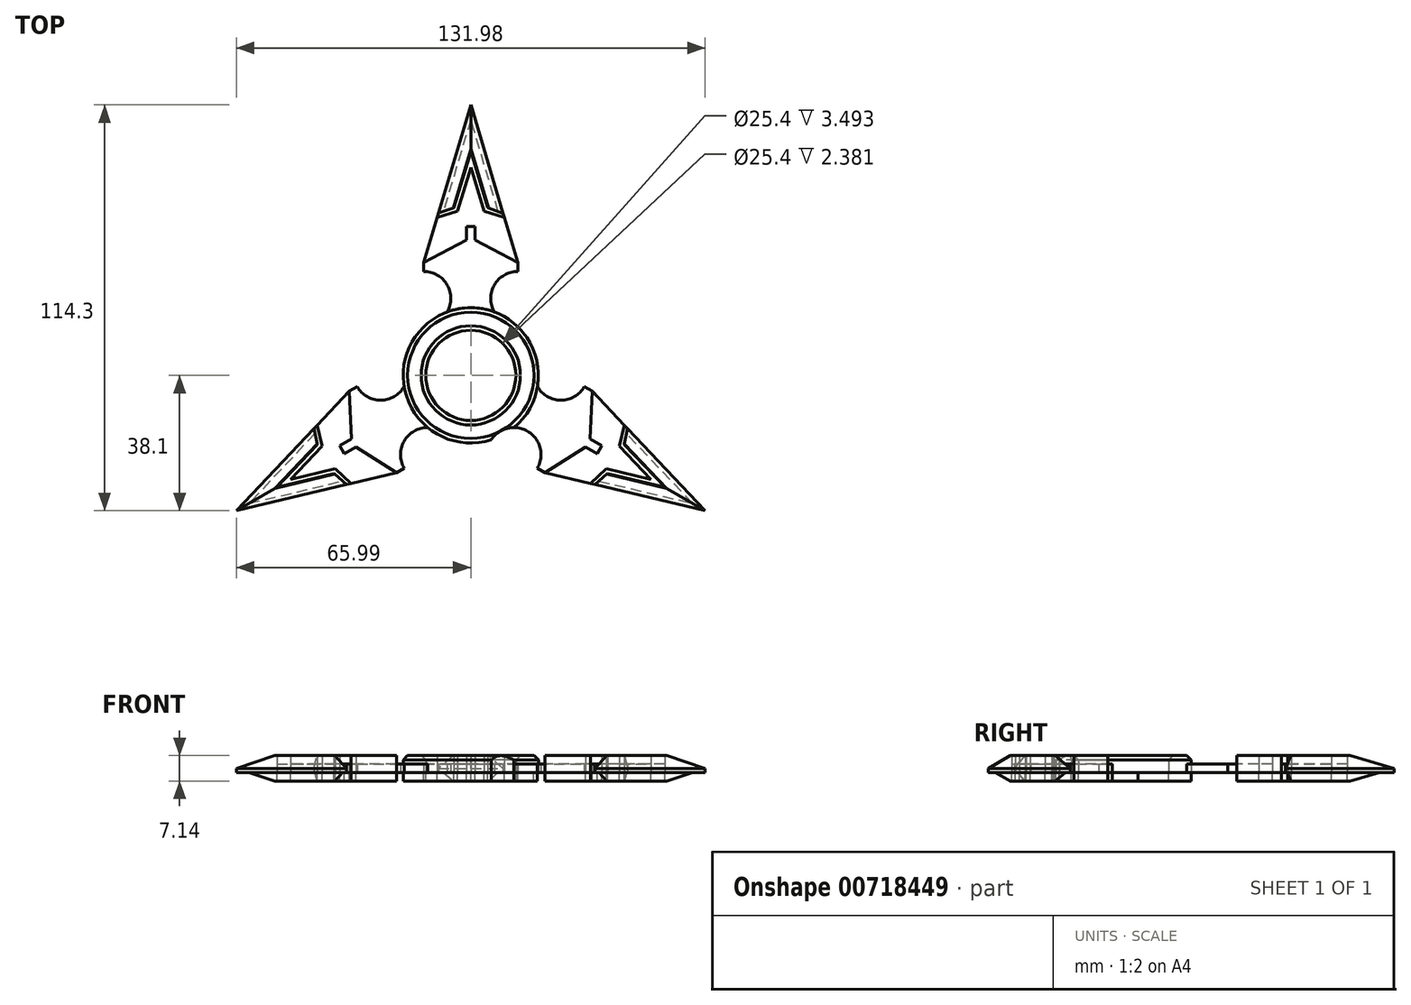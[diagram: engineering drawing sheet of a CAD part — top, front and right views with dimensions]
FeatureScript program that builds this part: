
annotation { "Feature Type Name" : "Feature", "Feature Type Description" : "" }
export const myFeature = defineFeature(function(context is Context, id is Id, definition is map)
    precondition{}
    {
        {
            var Q0;
            Q0=qCreatedBy(makeId("Top.planeOp"),FACE);
            var sketch = newSketch(context, id + "F0", { "sketchPlane" : qUnion([Q0])});
            skCircle(sketch, "E0", {"center": v(0, 0) * mm, "radius": 12.7 * mm});
            skCircle(sketch, "E1", {"center": v(0, 0) * mm, "radius": 19.05 * mm});
            skLineSegment(sketch, "E2", {"start": v(0, 76.2) * mm, "end": v(-13.25, 31.83) * mm});
            skLineSegment(sketch, "E3", {"start": v(13.25, 31.83) * mm, "end": v(0, 76.2) * mm});
            skLineSegment(sketch, "E4", {"start": v(-13.25, 31.83) * mm, "end": v(-13.25, 29.3) * mm});
            skLineSegment(sketch, "E5", {"start": v(13.25, 31.83) * mm, "end": v(13.25, 29.3) * mm});
            skLineSegment(sketch, "E6", {"start": v(0, 0) * mm, "end": v(-4, 18.62) * mm});
            skPoint(sketch, "E7", {"position": v(-12.85, 14.06) * mm});
            skPoint(sketch, "E8", {"position": v(12.85, 14.06) * mm});
            skArc(sketch, "E9", {"start": v(-12.85, 14.06) * mm, "mid": v(-5.63, 21.87) * mm, "end": v(-13.25, 29.3) * mm});
            skArc(sketch, "E10", {"start": v(13.25, 29.3) * mm, "mid": v(5.63, 21.87) * mm, "end": v(12.85, 14.06) * mm});
            skPoint(sketch, "E11", {"position": v(0, 63.05) * mm});
            skPoint(sketch, "E12", {"position": v(-4.73, 47.22) * mm});
            skPoint(sketch, "E13", {"position": v(4.73, 47.22) * mm});
            skPoint(sketch, "E14", {"position": v(-9.1, 45.72) * mm});
            skPoint(sketch, "E15", {"position": v(9.12, 45.67) * mm});
            skLineSegment(sketch, "E16", {"start": v(-9.1, 45.72) * mm, "end": v(-4.73, 47.22) * mm});
            skLineSegment(sketch, "E17", {"start": v(0, 63.05) * mm, "end": v(-4.73, 47.22) * mm});
            skLineSegment(sketch, "E18", {"start": v(0, 63.05) * mm, "end": v(4.73, 47.22) * mm});
            skLineSegment(sketch, "E19", {"start": v(4.73, 47.22) * mm, "end": v(9.12, 45.67) * mm});
            skPoint(sketch, "E20", {"position": v(-9.48, 44.45) * mm});
            skPoint(sketch, "E21", {"position": v(9.48, 44.45) * mm});
            skPoint(sketch, "E22", {"position": v(0, 58.62) * mm});
            skLineSegment(sketch, "E23", {"start": v(-13.25, 31.83) * mm, "end": v(-1.27, 38.1) * mm});
            skLineSegment(sketch, "E24", {"start": v(-1.27, 38.1) * mm, "end": v(-1.27, 41.91) * mm});
            skLineSegment(sketch, "E25", {"start": v(-1.27, 41.91) * mm, "end": v(1.27, 41.91) * mm});
            skLineSegment(sketch, "E26", {"start": v(1.27, 41.91) * mm, "end": v(1.27, 38.1) * mm});
            skLineSegment(sketch, "E27", {"start": v(1.27, 38.1) * mm, "end": v(13.25, 31.83) * mm});
            skLineSegment(sketch, "E28", {"start": v(-9.48, 44.45) * mm, "end": v(-3.7, 46.2) * mm});
            skLineSegment(sketch, "E29", {"start": v(-3.7, 46.2) * mm, "end": v(0, 58.62) * mm});
            skLineSegment(sketch, "E30", {"start": v(0, 58.62) * mm, "end": v(3.7, 46.2) * mm});
            skLineSegment(sketch, "E31", {"start": v(3.7, 46.2) * mm, "end": v(9.48, 44.45) * mm});
            skPoint(sketch, "E32.1.0", {"position": v(-43.23, -14.01) * mm});
            skLineSegment(sketch, "E32.1.1", {"start": v(-66, -38.1) * mm, "end": v(-20.94, -27.39) * mm});
            skLineSegment(sketch, "E32.1.2", {"start": v(-33.63, -17.95) * mm, "end": v(-34.2, -4.44) * mm});
            skPoint(sketch, "E32.1.3", {"position": v(-54.6, -31.53) * mm});
            skLineSegment(sketch, "E32.1.4", {"start": v(-20.94, -27.39) * mm, "end": v(-32.36, -20.15) * mm});
            skLineSegment(sketch, "E32.1.5", {"start": v(-34.2, -4.44) * mm, "end": v(-66, -38.1) * mm});
            skPoint(sketch, "E32.1.6", {"position": v(-33.75, -30.44) * mm});
            skLineSegment(sketch, "E32.1.7", {"start": v(-54.6, -31.53) * mm, "end": v(-38.52, -27.7) * mm});
            skPoint(sketch, "E32.1.8", {"position": v(-38.52, -27.7) * mm});
            skLineSegment(sketch, "E32.1.9", {"start": v(-50.76, -29.3) * mm, "end": v(-41.86, -19.89) * mm});
            skPoint(sketch, "E32.1.10", {"position": v(-44.1, -14.94) * mm});
            skLineSegment(sketch, "E32.1.11", {"start": v(-54.6, -31.53) * mm, "end": v(-43.25, -19.51) * mm});
            skPoint(sketch, "E32.1.12", {"position": v(-50.76, -29.3) * mm});
            skPoint(sketch, "E32.1.13", {"position": v(-43.25, -19.51) * mm});
            skPoint(sketch, "E32.1.14", {"position": v(-35.04, -30.74) * mm});
            skLineSegment(sketch, "E32.1.15", {"start": v(-38.15, -26.3) * mm, "end": v(-50.76, -29.3) * mm});
            skLineSegment(sketch, "E32.1.16", {"start": v(-41.86, -19.89) * mm, "end": v(-43.23, -14.01) * mm});
            skLineSegment(sketch, "E32.1.17", {"start": v(-36.93, -19.86) * mm, "end": v(-33.63, -17.95) * mm});
            skLineSegment(sketch, "E32.1.18", {"start": v(-43.25, -19.51) * mm, "end": v(-44.1, -14.94) * mm});
            skLineSegment(sketch, "E32.1.19", {"start": v(-33.75, -30.44) * mm, "end": v(-38.15, -26.3) * mm});
            skLineSegment(sketch, "E32.1.20", {"start": v(-35.04, -30.74) * mm, "end": v(-38.52, -27.7) * mm});
            skLineSegment(sketch, "E32.1.21", {"start": v(-35.66, -22.05) * mm, "end": v(-36.93, -19.86) * mm});
            skLineSegment(sketch, "E32.1.22", {"start": v(-32.36, -20.15) * mm, "end": v(-35.66, -22.05) * mm});
            skLineSegment(sketch, "E32.1.23", {"start": v(-34.2, -4.44) * mm, "end": v(-32, -3.17) * mm});
            skLineSegment(sketch, "E32.1.24", {"start": v(-20.94, -27.39) * mm, "end": v(-18.74, -26.12) * mm});
            skArc(sketch, "E32.1.25", {"start": v(-32, -3.17) * mm, "mid": v(-21.75, -6.06) * mm, "end": v(-18.6, 4.1) * mm});
            skArc(sketch, "E32.1.26", {"start": v(-5.75, -18.16) * mm, "mid": v(-16.12, -15.81) * mm, "end": v(-18.74, -26.12) * mm});
            skPoint(sketch, "E32.2.0", {"position": v(33.75, -30.44) * mm});
            skLineSegment(sketch, "E32.2.1", {"start": v(66, -38.1) * mm, "end": v(34.2, -4.44) * mm});
            skLineSegment(sketch, "E32.2.2", {"start": v(32.36, -20.15) * mm, "end": v(20.94, -27.39) * mm});
            skPoint(sketch, "E32.2.3", {"position": v(54.6, -31.53) * mm});
            skLineSegment(sketch, "E32.2.4", {"start": v(34.2, -4.44) * mm, "end": v(33.63, -17.95) * mm});
            skLineSegment(sketch, "E32.2.5", {"start": v(20.94, -27.39) * mm, "end": v(66, -38.1) * mm});
            skPoint(sketch, "E32.2.6", {"position": v(43.23, -14.01) * mm});
            skLineSegment(sketch, "E32.2.7", {"start": v(54.6, -31.53) * mm, "end": v(43.25, -19.51) * mm});
            skPoint(sketch, "E32.2.8", {"position": v(43.25, -19.51) * mm});
            skLineSegment(sketch, "E32.2.9", {"start": v(50.76, -29.3) * mm, "end": v(38.15, -26.3) * mm});
            skPoint(sketch, "E32.2.10", {"position": v(35, -30.73) * mm});
            skLineSegment(sketch, "E32.2.11", {"start": v(54.6, -31.53) * mm, "end": v(38.52, -27.7) * mm});
            skPoint(sketch, "E32.2.12", {"position": v(50.76, -29.3) * mm});
            skPoint(sketch, "E32.2.13", {"position": v(38.52, -27.7) * mm});
            skPoint(sketch, "E32.2.14", {"position": v(44.15, -14.98) * mm});
            skLineSegment(sketch, "E32.2.15", {"start": v(41.86, -19.89) * mm, "end": v(50.76, -29.3) * mm});
            skLineSegment(sketch, "E32.2.16", {"start": v(38.15, -26.3) * mm, "end": v(33.75, -30.44) * mm});
            skLineSegment(sketch, "E32.2.17", {"start": v(35.66, -22.05) * mm, "end": v(32.36, -20.15) * mm});
            skLineSegment(sketch, "E32.2.18", {"start": v(38.52, -27.7) * mm, "end": v(35, -30.73) * mm});
            skLineSegment(sketch, "E32.2.19", {"start": v(43.23, -14.01) * mm, "end": v(41.86, -19.89) * mm});
            skLineSegment(sketch, "E32.2.20", {"start": v(44.15, -14.98) * mm, "end": v(43.25, -19.51) * mm});
            skLineSegment(sketch, "E32.2.21", {"start": v(36.93, -19.86) * mm, "end": v(35.66, -22.05) * mm});
            skLineSegment(sketch, "E32.2.22", {"start": v(33.63, -17.95) * mm, "end": v(36.93, -19.86) * mm});
            skLineSegment(sketch, "E32.2.23", {"start": v(20.94, -27.39) * mm, "end": v(18.74, -26.12) * mm});
            skLineSegment(sketch, "E32.2.24", {"start": v(34.2, -4.44) * mm, "end": v(32, -3.17) * mm});
            skArc(sketch, "E32.2.25", {"start": v(18.74, -26.12) * mm, "mid": v(16.12, -15.81) * mm, "end": v(5.75, -18.16) * mm});
            skArc(sketch, "E32.2.26", {"start": v(18.6, 4.1) * mm, "mid": v(21.75, -6.06) * mm, "end": v(32, -3.17) * mm});
            skCircle(sketch, "E33", {"center": v(228.68, 14.43) * mm, "radius": 12.7 * mm});
            skCircle(sketch, "E34", {"center": v(228.68, 14.43) * mm, "radius": 19.05 * mm});
            skLineSegment(sketch, "E35", {"start": v(228.68, 90.63) * mm, "end": v(215.43, 46.27) * mm});
            skLineSegment(sketch, "E36", {"start": v(241.93, 46.27) * mm, "end": v(228.68, 90.63) * mm});
            skLineSegment(sketch, "E37", {"start": v(215.43, 46.27) * mm, "end": v(215.43, 43.73) * mm});
            skLineSegment(sketch, "E38", {"start": v(241.93, 46.27) * mm, "end": v(241.93, 43.73) * mm});
            skPoint(sketch, "E39", {"position": v(215.83, 28.5) * mm});
            skPoint(sketch, "E40", {"position": v(241.53, 28.5) * mm});
            skArc(sketch, "E41", {"start": v(215.83, 28.5) * mm, "mid": v(223.05, 36.3) * mm, "end": v(215.43, 43.73) * mm});
            skArc(sketch, "E42", {"start": v(241.93, 43.73) * mm, "mid": v(234.3, 36.3) * mm, "end": v(241.53, 28.5) * mm});
            skPoint(sketch, "E43", {"position": v(228.68, 77.49) * mm});
            skPoint(sketch, "E44", {"position": v(223.95, 61.65) * mm});
            skPoint(sketch, "E45", {"position": v(233.4, 61.65) * mm});
            skPoint(sketch, "E46", {"position": v(219.58, 60.15) * mm});
            skPoint(sketch, "E47", {"position": v(237.8, 60.1) * mm});
            skLineSegment(sketch, "E48", {"start": v(219.58, 60.15) * mm, "end": v(223.95, 61.65) * mm});
            skLineSegment(sketch, "E49", {"start": v(228.68, 77.49) * mm, "end": v(223.95, 61.65) * mm});
            skLineSegment(sketch, "E50", {"start": v(228.68, 77.49) * mm, "end": v(233.4, 61.65) * mm});
            skLineSegment(sketch, "E51", {"start": v(233.4, 61.65) * mm, "end": v(237.8, 60.1) * mm});
            skPoint(sketch, "E52", {"position": v(219.2, 58.88) * mm});
            skPoint(sketch, "E53", {"position": v(238.16, 58.88) * mm});
            skPoint(sketch, "E54", {"position": v(228.68, 73.05) * mm});
            skLineSegment(sketch, "E55", {"start": v(215.43, 46.27) * mm, "end": v(227.4, 52.53) * mm});
            skLineSegment(sketch, "E56", {"start": v(227.4, 52.53) * mm, "end": v(227.4, 56.34) * mm});
            skLineSegment(sketch, "E57", {"start": v(227.4, 56.34) * mm, "end": v(229.95, 56.34) * mm});
            skLineSegment(sketch, "E58", {"start": v(229.95, 56.34) * mm, "end": v(229.95, 52.53) * mm});
            skLineSegment(sketch, "E59", {"start": v(229.95, 52.53) * mm, "end": v(241.93, 46.27) * mm});
            skLineSegment(sketch, "E60", {"start": v(219.2, 58.88) * mm, "end": v(224.97, 60.63) * mm});
            skLineSegment(sketch, "E61", {"start": v(224.97, 60.63) * mm, "end": v(228.68, 73.05) * mm});
            skLineSegment(sketch, "E62", {"start": v(228.68, 73.05) * mm, "end": v(232.39, 60.63) * mm});
            skLineSegment(sketch, "E63", {"start": v(232.39, 60.63) * mm, "end": v(238.16, 58.88) * mm});
            skPoint(sketch, "E64.1.0", {"position": v(185.44, 0.42) * mm});
            skLineSegment(sketch, "E64.1.1", {"start": v(162.69, -23.67) * mm, "end": v(207.73, -12.95) * mm});
            skLineSegment(sketch, "E64.1.2", {"start": v(195.05, -3.52) * mm, "end": v(194.49, 10) * mm});
            skPoint(sketch, "E64.1.3", {"position": v(174.07, -17.1) * mm});
            skLineSegment(sketch, "E64.1.4", {"start": v(207.73, -12.95) * mm, "end": v(196.32, -5.72) * mm});
            skLineSegment(sketch, "E64.1.5", {"start": v(194.49, 10) * mm, "end": v(162.69, -23.67) * mm});
            skPoint(sketch, "E64.1.6", {"position": v(194.92, -16) * mm});
            skLineSegment(sketch, "E64.1.7", {"start": v(174.07, -17.1) * mm, "end": v(190.15, -13.27) * mm});
            skPoint(sketch, "E64.1.8", {"position": v(190.15, -13.27) * mm});
            skLineSegment(sketch, "E64.1.9", {"start": v(177.92, -14.87) * mm, "end": v(186.82, -5.45) * mm});
            skPoint(sketch, "E64.1.10", {"position": v(184.57, -0.5) * mm});
            skLineSegment(sketch, "E64.1.11", {"start": v(174.07, -17.1) * mm, "end": v(185.42, -5.08) * mm});
            skPoint(sketch, "E64.1.12", {"position": v(177.92, -14.87) * mm});
            skPoint(sketch, "E64.1.13", {"position": v(185.42, -5.08) * mm});
            skPoint(sketch, "E64.1.14", {"position": v(193.63, -16.3) * mm});
            skLineSegment(sketch, "E64.1.15", {"start": v(190.52, -11.88) * mm, "end": v(177.92, -14.87) * mm});
            skLineSegment(sketch, "E64.1.16", {"start": v(186.82, -5.45) * mm, "end": v(185.44, 0.42) * mm});
            skLineSegment(sketch, "E64.1.17", {"start": v(191.75, -5.42) * mm, "end": v(195.05, -3.52) * mm});
            skLineSegment(sketch, "E64.1.18", {"start": v(185.42, -5.08) * mm, "end": v(184.57, -0.5) * mm});
            skLineSegment(sketch, "E64.1.19", {"start": v(194.92, -16) * mm, "end": v(190.52, -11.88) * mm});
            skLineSegment(sketch, "E64.1.20", {"start": v(193.63, -16.3) * mm, "end": v(190.15, -13.27) * mm});
            skLineSegment(sketch, "E64.1.21", {"start": v(193.02, -7.62) * mm, "end": v(191.75, -5.42) * mm});
            skLineSegment(sketch, "E64.1.22", {"start": v(196.32, -5.72) * mm, "end": v(193.02, -7.62) * mm});
            skLineSegment(sketch, "E64.1.23", {"start": v(194.49, 10) * mm, "end": v(196.69, 11.26) * mm});
            skLineSegment(sketch, "E64.1.24", {"start": v(207.73, -12.95) * mm, "end": v(209.93, -11.68) * mm});
            skArc(sketch, "E64.1.25", {"start": v(196.69, 11.26) * mm, "mid": v(206.92, 8.38) * mm, "end": v(210.07, 18.53) * mm});
            skArc(sketch, "E64.1.26", {"start": v(222.93, -3.73) * mm, "mid": v(212.55, -1.38) * mm, "end": v(209.93, -11.68) * mm});
            skPoint(sketch, "E64.2.0", {"position": v(262.43, -16) * mm});
            skLineSegment(sketch, "E64.2.1", {"start": v(294.67, -23.67) * mm, "end": v(262.87, 10) * mm});
            skLineSegment(sketch, "E64.2.2", {"start": v(261.04, -5.72) * mm, "end": v(249.62, -12.95) * mm});
            skPoint(sketch, "E64.2.3", {"position": v(283.28, -17.1) * mm});
            skLineSegment(sketch, "E64.2.4", {"start": v(262.87, 10) * mm, "end": v(262.3, -3.52) * mm});
            skLineSegment(sketch, "E64.2.5", {"start": v(249.62, -12.95) * mm, "end": v(294.67, -23.67) * mm});
            skPoint(sketch, "E64.2.6", {"position": v(271.91, 0.42) * mm});
            skLineSegment(sketch, "E64.2.7", {"start": v(283.28, -17.1) * mm, "end": v(271.93, -5.08) * mm});
            skPoint(sketch, "E64.2.8", {"position": v(271.93, -5.08) * mm});
            skLineSegment(sketch, "E64.2.9", {"start": v(279.44, -14.87) * mm, "end": v(266.83, -11.88) * mm});
            skPoint(sketch, "E64.2.10", {"position": v(263.67, -16.3) * mm});
            skLineSegment(sketch, "E64.2.11", {"start": v(283.28, -17.1) * mm, "end": v(267.2, -13.27) * mm});
            skPoint(sketch, "E64.2.12", {"position": v(279.44, -14.87) * mm});
            skPoint(sketch, "E64.2.13", {"position": v(267.2, -13.27) * mm});
            skPoint(sketch, "E64.2.14", {"position": v(272.82, -0.54) * mm});
            skLineSegment(sketch, "E64.2.15", {"start": v(270.54, -5.45) * mm, "end": v(279.44, -14.87) * mm});
            skLineSegment(sketch, "E64.2.16", {"start": v(266.83, -11.88) * mm, "end": v(262.43, -16) * mm});
            skLineSegment(sketch, "E64.2.17", {"start": v(264.34, -7.62) * mm, "end": v(261.04, -5.72) * mm});
            skLineSegment(sketch, "E64.2.18", {"start": v(267.2, -13.27) * mm, "end": v(263.67, -16.3) * mm});
            skLineSegment(sketch, "E64.2.19", {"start": v(271.91, 0.42) * mm, "end": v(270.54, -5.45) * mm});
            skLineSegment(sketch, "E64.2.20", {"start": v(272.82, -0.54) * mm, "end": v(271.93, -5.08) * mm});
            skLineSegment(sketch, "E64.2.21", {"start": v(265.6, -5.42) * mm, "end": v(264.34, -7.62) * mm});
            skLineSegment(sketch, "E64.2.22", {"start": v(262.3, -3.52) * mm, "end": v(265.6, -5.42) * mm});
            skLineSegment(sketch, "E64.2.23", {"start": v(249.62, -12.95) * mm, "end": v(247.42, -11.68) * mm});
            skLineSegment(sketch, "E64.2.24", {"start": v(262.87, 10) * mm, "end": v(260.67, 11.26) * mm});
            skArc(sketch, "E64.2.25", {"start": v(247.42, -11.68) * mm, "mid": v(244.8, -1.38) * mm, "end": v(234.43, -3.73) * mm});
            skArc(sketch, "E64.2.26", {"start": v(247.28, 18.53) * mm, "mid": v(250.43, 8.38) * mm, "end": v(260.67, 11.26) * mm});
            skSolve(sketch);
        }
        {
            var Q0;
            Q0=makeQuery(id+"F0.imprint","IMPRINT",FACE,{"disambiguationData":[TD([[makeQuery(id+"F0.imprint","IMPRINT",EDGE,{"derivedFrom":sQuery(id+"F0.wireOp",EDGE,"E32.2.2")}),-1.0]])]});
            var Q1;
            Q1=makeQuery(id+"F0.imprint","IMPRINT",FACE,{"disambiguationData":[TD([[makeQuery(id+"F0.imprint","IMPRINT",EDGE,{"derivedFrom":sQuery(id+"F0.wireOp",EDGE,"E32.1.2")}),-1.0]])]});
            var Q2;
            {var subQ5=sQuery(id+"F0.wireOp",EDGE,"E4");Q2=makeQuery(id+"F0.imprint","IMPRINT",FACE,{"disambiguationData":[TD([[makeQuery(id+"F0.imprint","IMPRINT",EDGE,{"derivedFrom":subQ5}),1.0]])]});}
            var Q3;
            {var subQ1=sQuery(id+"F0.wireOp",EDGE,"E16");Q3=makeQuery(id+"F0.imprint","IMPRINT",FACE,{"disambiguationData":[TD([[makeQuery(id+"F0.imprint","IMPRINT",EDGE,{"derivedFrom":subQ1}),-1.0]])]});}
            var Q4;
            Q4=makeQuery(id+"F0.imprint","IMPRINT",FACE,{"disambiguationData":[TD([[makeQuery(id+"F0.imprint","IMPRINT",EDGE,{"derivedFrom":sQuery(id+"F0.wireOp",EDGE,"E32.2.7")}),1.0]])]});
            var Q5;
            Q5=makeQuery(id+"F0.imprint","IMPRINT",FACE,{"disambiguationData":[TD([[makeQuery(id+"F0.imprint","IMPRINT",EDGE,{"derivedFrom":sQuery(id+"F0.wireOp",EDGE,"E32.1.7")}),1.0]])]});
            extrude(context, id + "F1", {"entities" : qUnion([Q0, Q1, Q2, Q3, Q4, Q5]), "depth" : 2.38 * mm, "offsetDistance" : 25.4 * mm});
        }
        {
            var Q0;
            {var subQ2=sQuery(id+"F0.wireOp",EDGE,"E23");Q0=makeQuery(id+"F0.imprint","IMPRINT",FACE,{"disambiguationData":[TD([[makeQuery(id+"F0.imprint","IMPRINT",EDGE,{"derivedFrom":subQ2}),1.0]])]});}
            var Q1;
            {var subQ0=sQuery(id+"F0.wireOp",EDGE,"E16");Q1=makeQuery(id+"F0.imprint","IMPRINT",FACE,{"disambiguationData":[TD([[makeQuery(id+"F0.imprint","IMPRINT",EDGE,{"derivedFrom":subQ0}),1.0]])]});}
            var Q2;
            {var subQ4=sQuery(id+"F0.wireOp",EDGE,"E32.2.2");Q2=makeQuery(id+"F0.imprint","IMPRINT",FACE,{"disambiguationData":[TD([[makeQuery(id+"F0.imprint","IMPRINT",EDGE,{"derivedFrom":subQ4}),1.0]])]});}
            var Q3;
            Q3=makeQuery(id+"F0.imprint","IMPRINT",FACE,{"disambiguationData":[TD([[makeQuery(id+"F0.imprint","IMPRINT",EDGE,{"derivedFrom":sQuery(id+"F0.wireOp",EDGE,"E32.2.7")}),-1.0]])]});
            var Q4;
            Q4=makeQuery(id+"F0.imprint","IMPRINT",FACE,{"disambiguationData":[TD([[makeQuery(id+"F0.imprint","IMPRINT",EDGE,{"derivedFrom":sQuery(id+"F0.wireOp",EDGE,"E32.1.7")}),-1.0]])]});
            var Q5;
            {var subQ4=sQuery(id+"F0.wireOp",EDGE,"E32.1.2");Q5=makeQuery(id+"F0.imprint","IMPRINT",FACE,{"disambiguationData":[TD([[makeQuery(id+"F0.imprint","IMPRINT",EDGE,{"derivedFrom":subQ4}),1.0]])]});}
            var Q6;
            Q6=makeQuery(id+"F0.imprint","IMPRINT",FACE,{"disambiguationData":[TD([[makeQuery(id+"F0.imprint","IMPRINT",EDGE,{"derivedFrom":sQuery(id+"F0.wireOp",EDGE,"E0")}),-1.0]])]});
            var Q7;
            {var subQ0=sQuery(id+"F0.wireOp",EDGE,"E32.2.26");var subQ1=sQuery(id+"F0.wireOp",EDGE,"E1");var subQ2=makeQuery(id+"F0.imprint","INTERSECT",VERTEX,{"disambiguationData":[OD(0.0)],"derivedFrom":[subQ1,subQ0]});Q7=makeQuery(id+"F0.imprint","IMPRINT",FACE,{"disambiguationData":[TD([[makeQuery(id+"F0.imprint","IMPRINT",EDGE,{"disambiguationData":[TD([[subQ2,1.0]])],"derivedFrom":subQ1}),1.0]])]});}
            var Q8;
            {var subQ0=sQuery(id+"F0.wireOp",EDGE,"E32.2.25");var subQ1=sQuery(id+"F0.wireOp",EDGE,"E1");var subQ2=makeQuery(id+"F0.imprint","INTERSECT",VERTEX,{"disambiguationData":[OD(0.0)],"derivedFrom":[subQ1,subQ0]});Q8=makeQuery(id+"F0.imprint","IMPRINT",FACE,{"disambiguationData":[TD([[makeQuery(id+"F0.imprint","IMPRINT",EDGE,{"disambiguationData":[TD([[subQ2,-1.0]])],"derivedFrom":subQ1}),1.0]])]});}
            var Q9;
            {var subQ0=sQuery(id+"F0.wireOp",EDGE,"E32.1.26");var subQ1=sQuery(id+"F0.wireOp",EDGE,"E1");var subQ2=makeQuery(id+"F0.imprint","INTERSECT",VERTEX,{"disambiguationData":[OD(0.0)],"derivedFrom":[subQ1,subQ0]});Q9=makeQuery(id+"F0.imprint","IMPRINT",FACE,{"disambiguationData":[TD([[makeQuery(id+"F0.imprint","IMPRINT",EDGE,{"disambiguationData":[TD([[subQ2,1.0]])],"derivedFrom":subQ1}),1.0]])]});}
            var Q10;
            {var subQ0=sQuery(id+"F0.wireOp",EDGE,"E32.1.25");var subQ1=sQuery(id+"F0.wireOp",EDGE,"E1");var subQ2=makeQuery(id+"F0.imprint","INTERSECT",VERTEX,{"disambiguationData":[OD(0.0)],"derivedFrom":[subQ1,subQ0]});Q10=makeQuery(id+"F0.imprint","IMPRINT",FACE,{"disambiguationData":[TD([[makeQuery(id+"F0.imprint","IMPRINT",EDGE,{"disambiguationData":[TD([[subQ2,-1.0]])],"derivedFrom":subQ1}),1.0]])]});}
            var Q11;
            {var subQ0=sQuery(id+"F0.wireOp",EDGE,"E9");var subQ1=sQuery(id+"F0.wireOp",EDGE,"E1");var subQ2=makeQuery(id+"F0.imprint","INTERSECT",VERTEX,{"disambiguationData":[OD(0.0)],"derivedFrom":[subQ1,subQ0]});Q11=makeQuery(id+"F0.imprint","IMPRINT",FACE,{"disambiguationData":[TD([[makeQuery(id+"F0.imprint","IMPRINT",EDGE,{"disambiguationData":[TD([[subQ2,1.0]])],"derivedFrom":subQ1}),1.0]])]});}
            var Q12;
            {var subQ0=sQuery(id+"F0.wireOp",EDGE,"E10");var subQ1=sQuery(id+"F0.wireOp",EDGE,"E1");var subQ2=makeQuery(id+"F0.imprint","INTERSECT",VERTEX,{"disambiguationData":[OD(0.0)],"derivedFrom":[subQ1,subQ0]});Q12=makeQuery(id+"F0.imprint","IMPRINT",FACE,{"disambiguationData":[TD([[makeQuery(id+"F0.imprint","IMPRINT",EDGE,{"disambiguationData":[TD([[subQ2,-1.0]])],"derivedFrom":subQ1}),1.0]])]});}
            extrude(context, id + "F2", {"entities" : qUnion([Q0, Q1, Q2, Q3, Q4, Q5, Q6, Q7, Q8, Q9, Q10, Q11, Q12]), "depth" : 4.76 * mm, "offsetDistance" : 25.4 * mm});
        }
        {
            var Q0;
            Q0=makeQuery(id+"F0.imprint","IMPRINT",FACE,{"disambiguationData":[TD([[makeQuery(id+"F0.imprint","IMPRINT",EDGE,{"derivedFrom":sQuery(id+"F0.wireOp",EDGE,"E0")}),-1.0]])]});
            var Q1;
            {var subQ0=sQuery(id+"F0.wireOp",EDGE,"E32.2.25");var subQ1=sQuery(id+"F0.wireOp",EDGE,"E1");var subQ2=makeQuery(id+"F0.imprint","INTERSECT",VERTEX,{"disambiguationData":[OD(0.0)],"derivedFrom":[subQ1,subQ0]});Q1=makeQuery(id+"F0.imprint","IMPRINT",FACE,{"disambiguationData":[TD([[makeQuery(id+"F0.imprint","IMPRINT",EDGE,{"disambiguationData":[TD([[subQ2,-1.0]])],"derivedFrom":subQ1}),1.0]])]});}
            var Q2;
            {var subQ0=sQuery(id+"F0.wireOp",EDGE,"E32.1.26");var subQ1=sQuery(id+"F0.wireOp",EDGE,"E1");var subQ2=makeQuery(id+"F0.imprint","INTERSECT",VERTEX,{"disambiguationData":[OD(0.0)],"derivedFrom":[subQ1,subQ0]});Q2=makeQuery(id+"F0.imprint","IMPRINT",FACE,{"disambiguationData":[TD([[makeQuery(id+"F0.imprint","IMPRINT",EDGE,{"disambiguationData":[TD([[subQ2,1.0]])],"derivedFrom":subQ1}),1.0]])]});}
            var Q3;
            {var subQ0=sQuery(id+"F0.wireOp",EDGE,"E32.1.25");var subQ1=sQuery(id+"F0.wireOp",EDGE,"E1");var subQ2=makeQuery(id+"F0.imprint","INTERSECT",VERTEX,{"disambiguationData":[OD(0.0)],"derivedFrom":[subQ1,subQ0]});Q3=makeQuery(id+"F0.imprint","IMPRINT",FACE,{"disambiguationData":[TD([[makeQuery(id+"F0.imprint","IMPRINT",EDGE,{"disambiguationData":[TD([[subQ2,-1.0]])],"derivedFrom":subQ1}),1.0]])]});}
            var Q4;
            {var subQ0=sQuery(id+"F0.wireOp",EDGE,"E9");var subQ1=sQuery(id+"F0.wireOp",EDGE,"E1");var subQ2=makeQuery(id+"F0.imprint","INTERSECT",VERTEX,{"disambiguationData":[OD(0.0)],"derivedFrom":[subQ1,subQ0]});Q4=makeQuery(id+"F0.imprint","IMPRINT",FACE,{"disambiguationData":[TD([[makeQuery(id+"F0.imprint","IMPRINT",EDGE,{"disambiguationData":[TD([[subQ2,1.0]])],"derivedFrom":subQ1}),1.0]])]});}
            var Q5;
            {var subQ0=sQuery(id+"F0.wireOp",EDGE,"E10");var subQ1=sQuery(id+"F0.wireOp",EDGE,"E1");var subQ2=makeQuery(id+"F0.imprint","INTERSECT",VERTEX,{"disambiguationData":[OD(0.0)],"derivedFrom":[subQ1,subQ0]});Q5=makeQuery(id+"F0.imprint","IMPRINT",FACE,{"disambiguationData":[TD([[makeQuery(id+"F0.imprint","IMPRINT",EDGE,{"disambiguationData":[TD([[subQ2,-1.0]])],"derivedFrom":subQ1}),1.0]])]});}
            var Q6;
            {var subQ4=sQuery(id+"F0.wireOp",EDGE,"E32.2.2");Q6=makeQuery(id+"F0.imprint","IMPRINT",FACE,{"disambiguationData":[TD([[makeQuery(id+"F0.imprint","IMPRINT",EDGE,{"derivedFrom":subQ4}),1.0]])]});}
            var Q7;
            Q7=makeQuery(id+"F0.imprint","IMPRINT",FACE,{"disambiguationData":[TD([[makeQuery(id+"F0.imprint","IMPRINT",EDGE,{"derivedFrom":sQuery(id+"F0.wireOp",EDGE,"E32.2.7")}),-1.0]])]});
            var Q8;
            {var subQ4=sQuery(id+"F0.wireOp",EDGE,"E32.1.2");Q8=makeQuery(id+"F0.imprint","IMPRINT",FACE,{"disambiguationData":[TD([[makeQuery(id+"F0.imprint","IMPRINT",EDGE,{"derivedFrom":subQ4}),1.0]])]});}
            var Q9;
            Q9=makeQuery(id+"F0.imprint","IMPRINT",FACE,{"disambiguationData":[TD([[makeQuery(id+"F0.imprint","IMPRINT",EDGE,{"derivedFrom":sQuery(id+"F0.wireOp",EDGE,"E32.1.7")}),-1.0]])]});
            var Q10;
            {var subQ2=sQuery(id+"F0.wireOp",EDGE,"E23");Q10=makeQuery(id+"F0.imprint","IMPRINT",FACE,{"disambiguationData":[TD([[makeQuery(id+"F0.imprint","IMPRINT",EDGE,{"derivedFrom":subQ2}),1.0]])]});}
            var Q11;
            {var subQ0=sQuery(id+"F0.wireOp",EDGE,"E16");Q11=makeQuery(id+"F0.imprint","IMPRINT",FACE,{"disambiguationData":[TD([[makeQuery(id+"F0.imprint","IMPRINT",EDGE,{"derivedFrom":subQ0}),1.0]])]});}
            extrude(context, id + "F3", {"entities" : qUnion([Q0, Q1, Q2, Q3, Q4, Q5, Q6, Q7, Q8, Q9, Q10, Q11]), "oppositeDirection" : true, "depth" : 2.38 * mm, "offsetDistance" : 25.4 * mm});
        }
        {
            var Q0;
            {var subQ0=sQuery(id+"F0.wireOp",EDGE,"E32.1.1");Q0=makeQuery(id+"F2.opExtrude","CAP_EDGE",EDGE,{"disambiguationData":[OSD([subQ0]),TDD([makeQuery(id+"F0.imprint","IMPRINT",EDGE,{"disambiguationData":[TD([[makeQuery(id+"F0.imprint","INTERSECT",VERTEX,{"derivedFrom":[subQ0,sQuery(id+"F0.wireOp",EDGE,"E32.1.5")]}),-1.0]])],"derivedFrom":subQ0})])],"isStart":false});}
            var Q1;
            {var subQ0=sQuery(id+"F0.wireOp",EDGE,"E32.1.1");Q1=makeQuery(id+"F3.opExtrude","CAP_EDGE",EDGE,{"disambiguationData":[OSD([subQ0]),TDD([makeQuery(id+"F0.imprint","IMPRINT",EDGE,{"disambiguationData":[TD([[makeQuery(id+"F0.imprint","INTERSECT",VERTEX,{"derivedFrom":[subQ0,sQuery(id+"F0.wireOp",EDGE,"E32.1.5")]}),-1.0]])],"derivedFrom":subQ0})])],"isStart":false});}
            var Q2;
            {var subQ0=sQuery(id+"F0.wireOp",EDGE,"E32.1.5");Q2=makeQuery(id+"F2.opExtrude","CAP_EDGE",EDGE,{"disambiguationData":[OSD([subQ0]),TDD([makeQuery(id+"F0.imprint","IMPRINT",EDGE,{"disambiguationData":[TD([[makeQuery(id+"F0.imprint","INTERSECT",VERTEX,{"derivedFrom":[sQuery(id+"F0.wireOp",EDGE,"E32.1.1"),subQ0]}),1.0]])],"derivedFrom":subQ0})])],"isStart":false});}
            var Q3;
            {var subQ0=sQuery(id+"F0.wireOp",EDGE,"E32.1.5");Q3=makeQuery(id+"F3.opExtrude","CAP_EDGE",EDGE,{"disambiguationData":[OSD([subQ0]),TDD([makeQuery(id+"F0.imprint","IMPRINT",EDGE,{"disambiguationData":[TD([[makeQuery(id+"F0.imprint","INTERSECT",VERTEX,{"derivedFrom":[sQuery(id+"F0.wireOp",EDGE,"E32.1.1"),subQ0]}),1.0]])],"derivedFrom":subQ0})])],"isStart":false});}
            var Q4;
            {var subQ0=sQuery(id+"F0.wireOp",EDGE,"E32.2.5");Q4=makeQuery(id+"F2.opExtrude","CAP_EDGE",EDGE,{"disambiguationData":[OSD([subQ0]),TDD([makeQuery(id+"F0.imprint","IMPRINT",EDGE,{"disambiguationData":[TD([[makeQuery(id+"F0.imprint","INTERSECT",VERTEX,{"derivedFrom":[sQuery(id+"F0.wireOp",EDGE,"E32.2.1"),subQ0]}),1.0]])],"derivedFrom":subQ0})])],"isStart":false});}
            var Q5;
            {var subQ0=sQuery(id+"F0.wireOp",EDGE,"E32.2.5");Q5=makeQuery(id+"F3.opExtrude","CAP_EDGE",EDGE,{"disambiguationData":[OSD([subQ0]),TDD([makeQuery(id+"F0.imprint","IMPRINT",EDGE,{"disambiguationData":[TD([[makeQuery(id+"F0.imprint","INTERSECT",VERTEX,{"derivedFrom":[sQuery(id+"F0.wireOp",EDGE,"E32.2.1"),subQ0]}),1.0]])],"derivedFrom":subQ0})])],"isStart":false});}
            var Q6;
            {var subQ0=sQuery(id+"F0.wireOp",EDGE,"E32.2.1");Q6=makeQuery(id+"F2.opExtrude","CAP_EDGE",EDGE,{"disambiguationData":[OSD([subQ0]),TDD([makeQuery(id+"F0.imprint","IMPRINT",EDGE,{"disambiguationData":[TD([[makeQuery(id+"F0.imprint","INTERSECT",VERTEX,{"derivedFrom":[subQ0,sQuery(id+"F0.wireOp",EDGE,"E32.2.5")]}),-1.0]])],"derivedFrom":subQ0})])],"isStart":false});}
            var Q7;
            {var subQ0=sQuery(id+"F0.wireOp",EDGE,"E32.2.1");Q7=makeQuery(id+"F3.opExtrude","CAP_EDGE",EDGE,{"disambiguationData":[OSD([subQ0]),TDD([makeQuery(id+"F0.imprint","IMPRINT",EDGE,{"disambiguationData":[TD([[makeQuery(id+"F0.imprint","INTERSECT",VERTEX,{"derivedFrom":[subQ0,sQuery(id+"F0.wireOp",EDGE,"E32.2.5")]}),-1.0]])],"derivedFrom":subQ0})])],"isStart":false});}
            var Q8;
            {var subQ0=sQuery(id+"F0.wireOp",EDGE,"E3");Q8=makeQuery(id+"F2.opExtrude","CAP_EDGE",EDGE,{"disambiguationData":[OSD([subQ0]),TDD([makeQuery(id+"F0.imprint","IMPRINT",EDGE,{"disambiguationData":[TD([[makeQuery(id+"F0.imprint","INTERSECT",VERTEX,{"derivedFrom":[sQuery(id+"F0.wireOp",EDGE,"E2"),subQ0]}),1.0]])],"derivedFrom":subQ0})])],"isStart":false});}
            var Q9;
            {var subQ0=sQuery(id+"F0.wireOp",EDGE,"E3");Q9=makeQuery(id+"F3.opExtrude","CAP_EDGE",EDGE,{"disambiguationData":[OSD([subQ0]),TDD([makeQuery(id+"F0.imprint","IMPRINT",EDGE,{"disambiguationData":[TD([[makeQuery(id+"F0.imprint","INTERSECT",VERTEX,{"derivedFrom":[sQuery(id+"F0.wireOp",EDGE,"E2"),subQ0]}),1.0]])],"derivedFrom":subQ0})])],"isStart":false});}
            var Q10;
            {var subQ0=sQuery(id+"F0.wireOp",EDGE,"E2");Q10=makeQuery(id+"F3.opExtrude","CAP_EDGE",EDGE,{"disambiguationData":[OSD([subQ0]),TDD([makeQuery(id+"F0.imprint","IMPRINT",EDGE,{"disambiguationData":[TD([[makeQuery(id+"F0.imprint","INTERSECT",VERTEX,{"derivedFrom":[subQ0,sQuery(id+"F0.wireOp",EDGE,"E3")]}),-1.0]])],"derivedFrom":subQ0})])],"isStart":false});}
            var Q11;
            {var subQ0=sQuery(id+"F0.wireOp",EDGE,"E2");Q11=makeQuery(id+"F2.opExtrude","CAP_EDGE",EDGE,{"disambiguationData":[OSD([subQ0]),TDD([makeQuery(id+"F0.imprint","IMPRINT",EDGE,{"disambiguationData":[TD([[makeQuery(id+"F0.imprint","INTERSECT",VERTEX,{"derivedFrom":[subQ0,sQuery(id+"F0.wireOp",EDGE,"E3")]}),-1.0]])],"derivedFrom":subQ0})])],"isStart":false});}
            chamfer(context, id + "F4", {"entities" : qUnion([Q0, Q1, Q2, Q3, Q4, Q5, Q6, Q7, Q8, Q9, Q10, Q11]), "width" : 3.57 * mm, "tangentPropagation" : true});
        }
        {
            var Q0;
            Q0=makeQuery(id+"F2.opExtrude","CAP_EDGE",EDGE,{"disambiguationData":[OSD([sQuery(id+"F0.wireOp",EDGE,"E1")])],"isStart":false});
            var Q1;
            Q1=makeQuery(id+"F2.opExtrude","CAP_EDGE",EDGE,{"disambiguationData":[OSD([sQuery(id+"F0.wireOp",EDGE,"E0")])],"isStart":false});
            chamfer(context, id + "F5", {"entities" : qUnion([Q0, Q1]), "width" : 1.27 * mm, "tangentPropagation" : true});
        }
    });
